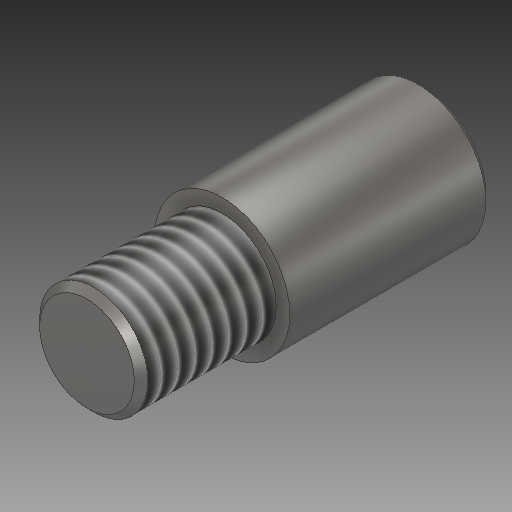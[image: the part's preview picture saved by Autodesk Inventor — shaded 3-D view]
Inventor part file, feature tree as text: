
AUTODESK INVENTOR PART (.ipt)
format: ipt  version: 2018 (Build 220112000, 112)  size: 164,864 bytes
history: native  units: mm
features: extrude x2, sketch x2, thread x1, chamfer x1
ambient origin geometry x8: Origin, YZ Plane, XZ Plane, XY Plane, X Axis, Y Axis, Z Axis, Center Point
bodies: Solido1 (feature_tree)
feature tree (6):
  extrude  "Estrusione1"  Depth=10.0mm
  extrude  "Estrusione2"  Depth=15.0mm TaperAngle=0.0deg
  thread  "Filettatura1"
  chamfer  "Smusso1"  Distance=8.0mm
  sketch  "Schizzo1"
  sketch  "Schizzo2"
